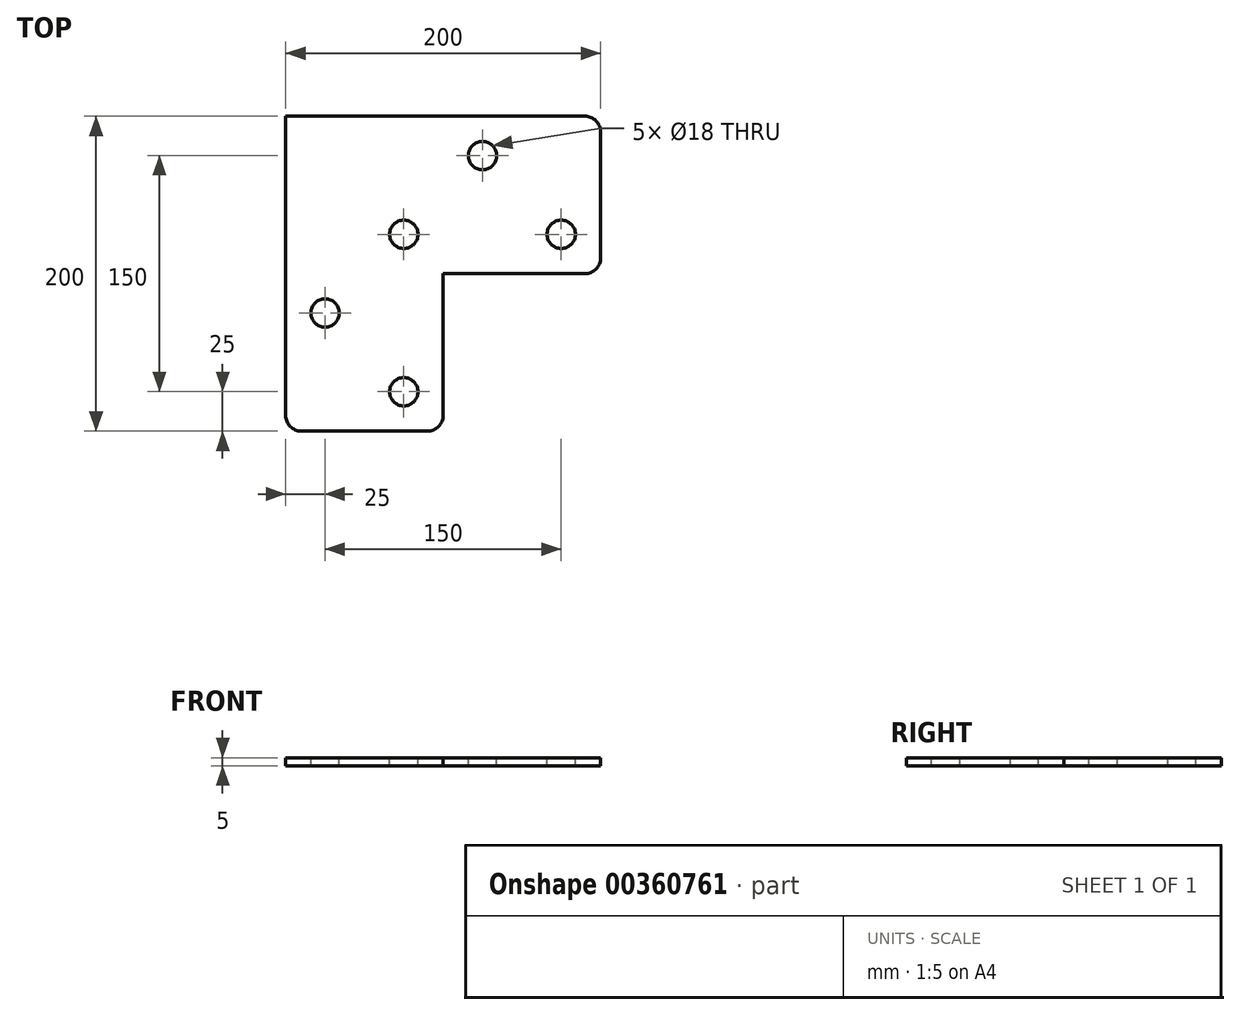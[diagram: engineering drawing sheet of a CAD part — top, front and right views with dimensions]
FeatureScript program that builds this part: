
annotation { "Feature Type Name" : "Feature", "Feature Type Description" : "" }
export const myFeature = defineFeature(function(context is Context, id is Id, definition is map)
    precondition{}
    {
        {
            var Q0;
            Q0=qCreatedBy(makeId("Top.planeOp"),FACE);
            var sketch = newSketch(context, id + "F0", { "sketchPlane" : qUnion([Q0])});
            skLineSegment(sketch, "E0", {"start": v(0, 0) * mm, "end": v(200, 0) * mm});
            skLineSegment(sketch, "E1", {"start": v(200, 0) * mm, "end": v(200, -100) * mm});
            skLineSegment(sketch, "E2", {"start": v(200, -100) * mm, "end": v(100, -100) * mm});
            skLineSegment(sketch, "E3", {"start": v(100, -100) * mm, "end": v(100, -200) * mm});
            skLineSegment(sketch, "E4", {"start": v(100, -200) * mm, "end": v(0, -200) * mm});
            skLineSegment(sketch, "E5", {"start": v(0, -200) * mm, "end": v(0, 0) * mm});
            skSolve(sketch);
        }
        {
            var Q0;
            Q0=makeQuery(id+"F0.imprint","IMPRINT",FACE,{"disambiguationData":[TD([[makeQuery(id+"F0.imprint","IMPRINT",EDGE,{"derivedFrom":sQuery(id+"F0.wireOp",EDGE,"E0")}),-1.0]])]});
            extrude(context, id + "F1", {"entities" : qUnion([Q0]), "depth" : 5 * mm});
        }
        {
            var Q0;
            Q0=makeQuery(id+"F1.opExtrude","CAP_FACE",FACE,{"disambiguationData":[OSD([sQuery(id+"F0.wireOp",EDGE,"E0"),sQuery(id+"F0.wireOp",EDGE,"E1"),sQuery(id+"F0.wireOp",EDGE,"E2"),sQuery(id+"F0.wireOp",EDGE,"E3"),sQuery(id+"F0.wireOp",EDGE,"E4"),sQuery(id+"F0.wireOp",EDGE,"E5")])],"isStart":false});
            var sketch = newSketch(context, id + "F2", { "sketchPlane" : qUnion([Q0])});
            skLineSegment(sketch, "E6.direction2", {"start": v(175, -25) * mm, "end": v(175, -75) * mm, "construction": true});
            skPoint(sketch, "E7.startSnap0", {"position": v(175, -50) * mm});
            skCircle(sketch, "E8.MirrorC", {"center": v(175, -75) * mm, "radius": 9 * mm});
            skCircle(sketch, "E9.MirrorC", {"center": v(125, -25) * mm, "radius": 9 * mm});
            skCircle(sketch, "E10.MirrorC", {"center": v(75, -75) * mm, "radius": 9 * mm});
            skCircle(sketch, "E11.MirrorC", {"center": v(75, -175) * mm, "radius": 9 * mm});
            skCircle(sketch, "E12.MirrorC", {"center": v(25, -125) * mm, "radius": 9 * mm});
            skLineSegment(sketch, "E13", {"start": v(-0.08, 0) * mm, "end": v(-51.97, 0) * mm});
            skLineSegment(sketch, "E14", {"start": v(-0.08, 0) * mm, "end": v(-0.08, 38.5) * mm});
            skSolve(sketch);
        }
        {
            var Q0;
            Q0=qSketchRegion(id+"F2",true);
            extrude(context, id + "F3", {"entities" : qUnion([Q0]), "operationType" : NewBodyOperationType.REMOVE, "oppositeDirection" : true, "depth" : 25 * mm});
        }
        {
            var Q0;
            Q0=makeQuery(id+"F1.opExtrude","SWEPT_EDGE",EDGE,{"disambiguationData":[OSD([sQuery(id+"F0.wireOp",EDGE,"E4"),sQuery(id+"F0.wireOp",EDGE,"E5")])]});
            var Q1;
            Q1=makeQuery(id+"F1.opExtrude","SWEPT_EDGE",EDGE,{"disambiguationData":[OSD([sQuery(id+"F0.wireOp",EDGE,"E3"),sQuery(id+"F0.wireOp",EDGE,"E4")])]});
            var Q2;
            Q2=makeQuery(id+"F1.opExtrude","SWEPT_EDGE",EDGE,{"disambiguationData":[OSD([sQuery(id+"F0.wireOp",EDGE,"E1"),sQuery(id+"F0.wireOp",EDGE,"E2")])]});
            var Q3;
            Q3=makeQuery(id+"F1.opExtrude","SWEPT_EDGE",EDGE,{"disambiguationData":[OSD([sQuery(id+"F0.wireOp",EDGE,"E0"),sQuery(id+"F0.wireOp",EDGE,"E1")])]});
            fillet(context, id + "F4", {"entities" : qUnion([Q0, Q1, Q2, Q3]), "radius" : 10 * mm, "tangentPropagation" : true, "allowEdgeOverflow" : false});
        }
    });
